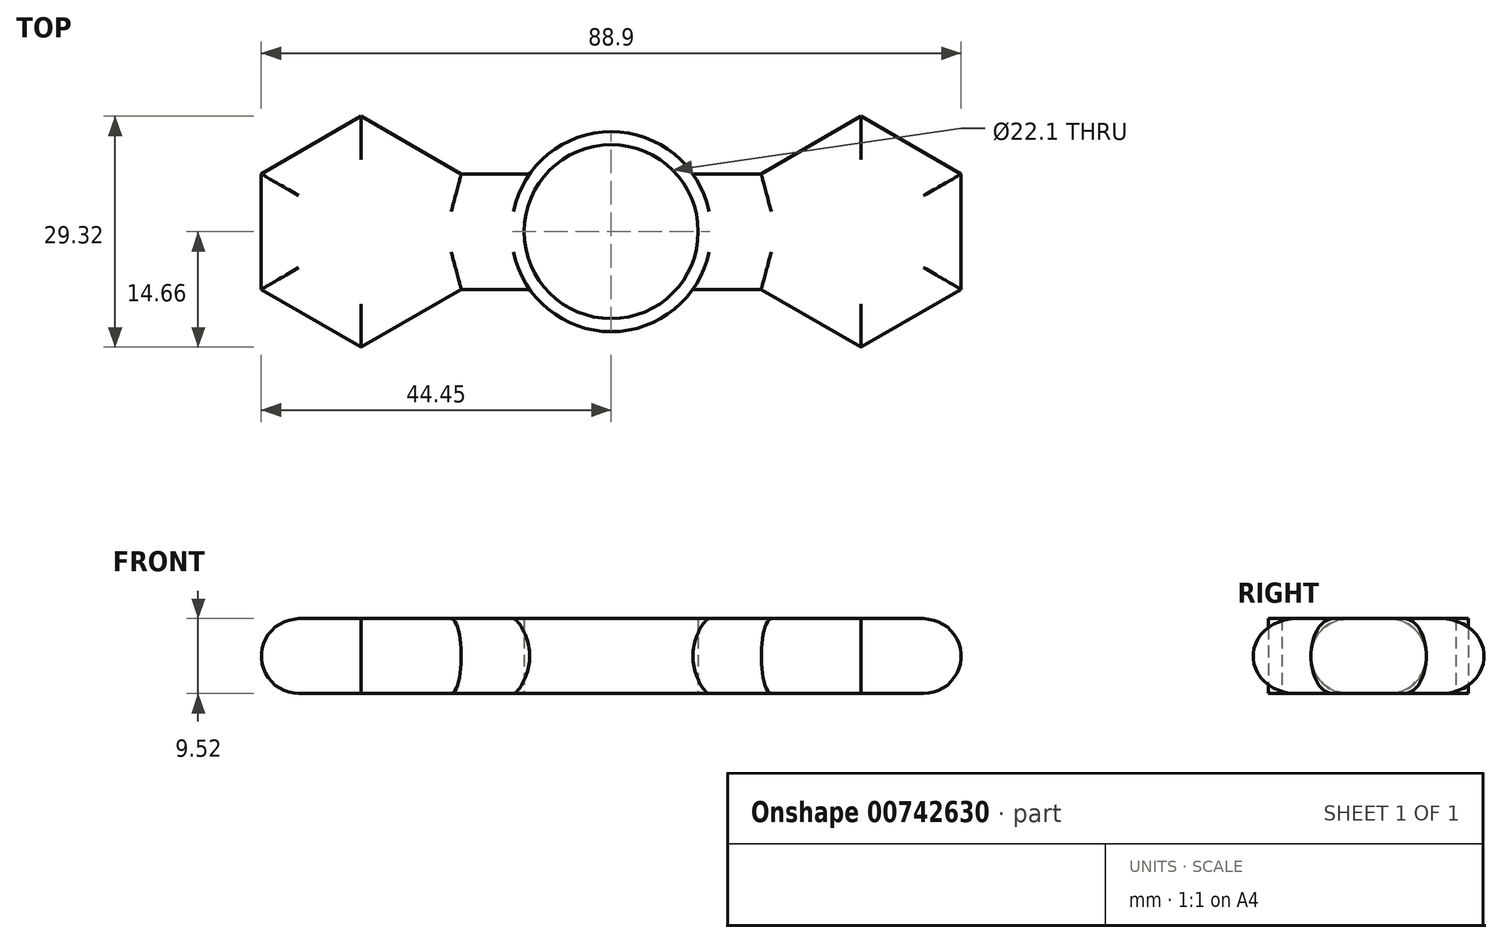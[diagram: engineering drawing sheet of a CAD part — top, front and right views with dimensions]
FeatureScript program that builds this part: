
annotation { "Feature Type Name" : "Feature", "Feature Type Description" : "" }
export const myFeature = defineFeature(function(context is Context, id is Id, definition is map)
    precondition{}
    {
        {
            var Q0;
            Q0=qCreatedBy(makeId("Top.planeOp"),FACE);
            var sketch = newSketch(context, id + "F0", { "sketchPlane" : qUnion([Q0])});
            skCircle(sketch, "E0", {"center": v(0, 0) * mm, "radius": 12.7 * mm});
            skCircle(sketch, "E1", {"center": v(0, 0) * mm, "radius": 11.05 * mm});
            skSolve(sketch);
        }
        {
            var Q0;
            Q0 = qSketchRegion(id + "F0", true);
            extrude(context, id + "F1", {"entities" : qUnion([Q0]), "endBound" : BoundingType.SYMMETRIC, "depth" : 9.52 * mm, "offsetDistance" : 25.4 * mm});
        }
        {
            var Q0;
            Q0=qCreatedBy(makeId("Top.planeOp"),FACE);
            var sketch = newSketch(context, id + "F2", { "sketchPlane" : qUnion([Q0])});
            skArc(sketch, "E2", {"start": v(-10.37, 7.33) * mm, "mid": v(-12.7, 0) * mm, "end": v(-10.37, -7.33) * mm});
            skLineSegment(sketch, "E3.1", {"start": v(-19.05, -7.33) * mm, "end": v(-31.75, -14.66) * mm});
            skLineSegment(sketch, "E3.2", {"start": v(-31.75, -14.66) * mm, "end": v(-44.45, -7.33) * mm});
            skLineSegment(sketch, "E3.3", {"start": v(-44.45, -7.33) * mm, "end": v(-44.45, 7.33) * mm});
            skLineSegment(sketch, "E3.4", {"start": v(-44.45, 7.33) * mm, "end": v(-31.75, 14.66) * mm});
            skLineSegment(sketch, "E3.5", {"start": v(-31.75, 14.66) * mm, "end": v(-19.05, 7.33) * mm});
            skLineSegment(sketch, "E4.MirrorCS", {"start": v(44.45, 7.33) * mm, "end": v(31.75, 14.66) * mm});
            skLineSegment(sketch, "E5.MirrorCS", {"start": v(31.75, 14.66) * mm, "end": v(19.05, 7.33) * mm});
            skLineSegment(sketch, "E6.MirrorCS", {"start": v(44.45, -7.33) * mm, "end": v(44.45, 7.33) * mm});
            skLineSegment(sketch, "E7.MirrorCS", {"start": v(31.75, -14.66) * mm, "end": v(44.45, -7.33) * mm});
            skLineSegment(sketch, "E8.MirrorCS", {"start": v(19.05, -7.33) * mm, "end": v(31.75, -14.66) * mm});
            skLineSegment(sketch, "E9", {"start": v(19.05, 7.33) * mm, "end": v(10.37, 7.33) * mm});
            skLineSegment(sketch, "E10", {"start": v(19.05, -7.33) * mm, "end": v(10.37, -7.33) * mm});
            skLineSegment(sketch, "E11", {"start": v(-19.05, 7.33) * mm, "end": v(-10.37, 7.33) * mm});
            skLineSegment(sketch, "E12", {"start": v(-19.05, -7.33) * mm, "end": v(-10.37, -7.33) * mm});
            skArc(sketch, "E13.trimOffspring", {"start": v(10.37, -7.33) * mm, "mid": v(12.7, 0) * mm, "end": v(10.37, 7.33) * mm});
            skSolve(sketch);
        }
        {
            var Q0;
            Q0 = qSketchRegion(id + "F2", true);
            extrude(context, id + "F3", {"entities" : qUnion([Q0]), "operationType" : NewBodyOperationType.ADD, "endBound" : BoundingType.SYMMETRIC, "depth" : 9.52 * mm, "offsetDistance" : 25.4 * mm});
        }
        {
            var Q0;
            Q0=makeQuery(id+"F3.opExtrude","CAP_EDGE",EDGE,{"disambiguationData":[OSD([sQuery(id+"F2.wireOp",EDGE,"E7.MirrorCS")])],"isStart":false});
            var Q1;
            Q1=makeQuery(id+"F3.opExtrude","CAP_EDGE",EDGE,{"disambiguationData":[OSD([sQuery(id+"F2.wireOp",EDGE,"E6.MirrorCS")])],"isStart":false});
            var Q2;
            Q2=makeQuery(id+"F3.opExtrude","CAP_EDGE",EDGE,{"disambiguationData":[OSD([sQuery(id+"F2.wireOp",EDGE,"E8.MirrorCS")])],"isStart":false});
            var Q3;
            Q3=makeQuery(id+"F3.opExtrude","CAP_EDGE",EDGE,{"disambiguationData":[OSD([sQuery(id+"F2.wireOp",EDGE,"E10")])],"isStart":false});
            var Q4;
            Q4=makeQuery(id+"F3.opExtrude","CAP_EDGE",EDGE,{"disambiguationData":[OSD([sQuery(id+"F2.wireOp",EDGE,"E9")])],"isStart":false});
            var Q5;
            Q5=makeQuery(id+"F3.opExtrude","CAP_EDGE",EDGE,{"disambiguationData":[OSD([sQuery(id+"F2.wireOp",EDGE,"E5.MirrorCS")])],"isStart":false});
            var Q6;
            Q6=makeQuery(id+"F3.opExtrude","CAP_EDGE",EDGE,{"disambiguationData":[OSD([sQuery(id+"F2.wireOp",EDGE,"E4.MirrorCS")])],"isStart":false});
            var Q7;
            Q7=makeQuery(id+"F3.opExtrude","CAP_EDGE",EDGE,{"disambiguationData":[OSD([sQuery(id+"F2.wireOp",EDGE,"E10")])],"isStart":true});
            var Q8;
            Q8=makeQuery(id+"F3.opExtrude","CAP_EDGE",EDGE,{"disambiguationData":[OSD([sQuery(id+"F2.wireOp",EDGE,"E8.MirrorCS")])],"isStart":true});
            var Q9;
            Q9=makeQuery(id+"F3.opExtrude","CAP_EDGE",EDGE,{"disambiguationData":[OSD([sQuery(id+"F2.wireOp",EDGE,"E7.MirrorCS")])],"isStart":true});
            var Q10;
            Q10=makeQuery(id+"F3.opExtrude","CAP_EDGE",EDGE,{"disambiguationData":[OSD([sQuery(id+"F2.wireOp",EDGE,"E6.MirrorCS")])],"isStart":true});
            var Q11;
            Q11=makeQuery(id+"F3.opExtrude","CAP_EDGE",EDGE,{"disambiguationData":[OSD([sQuery(id+"F2.wireOp",EDGE,"E9")])],"isStart":true});
            var Q12;
            Q12=makeQuery(id+"F3.opExtrude","CAP_EDGE",EDGE,{"disambiguationData":[OSD([sQuery(id+"F2.wireOp",EDGE,"E5.MirrorCS")])],"isStart":true});
            var Q13;
            Q13=makeQuery(id+"F3.opExtrude","CAP_EDGE",EDGE,{"disambiguationData":[OSD([sQuery(id+"F2.wireOp",EDGE,"E4.MirrorCS")])],"isStart":true});
            fillet(context, id + "F4", {"entities" : qUnion([Q0, Q1, Q2, Q3, Q4, Q5, Q6, Q7, Q8, Q9, Q10, Q11, Q12, Q13]), "radius" : 4.76 * mm, "tangentPropagation" : true, "allowEdgeOverflow" : false});
        }
        {
            var Q0;
            Q0=makeQuery(id+"F3.opExtrude","CAP_EDGE",EDGE,{"disambiguationData":[OSD([sQuery(id+"F2.wireOp",EDGE,"E3.4")])],"isStart":false});
            var Q1;
            Q1=makeQuery(id+"F3.opExtrude","CAP_EDGE",EDGE,{"disambiguationData":[OSD([sQuery(id+"F2.wireOp",EDGE,"E3.5")])],"isStart":false});
            var Q2;
            Q2=makeQuery(id+"F3.opExtrude","CAP_EDGE",EDGE,{"disambiguationData":[OSD([sQuery(id+"F2.wireOp",EDGE,"E11")])],"isStart":false});
            var Q3;
            Q3=makeQuery(id+"F3.opExtrude","CAP_EDGE",EDGE,{"disambiguationData":[OSD([sQuery(id+"F2.wireOp",EDGE,"E12")])],"isStart":false});
            var Q4;
            Q4=makeQuery(id+"F3.opExtrude","CAP_EDGE",EDGE,{"disambiguationData":[OSD([sQuery(id+"F2.wireOp",EDGE,"E3.1")])],"isStart":false});
            var Q5;
            Q5=makeQuery(id+"F3.opExtrude","CAP_EDGE",EDGE,{"disambiguationData":[OSD([sQuery(id+"F2.wireOp",EDGE,"E3.2")])],"isStart":false});
            var Q6;
            Q6=makeQuery(id+"F3.opExtrude","CAP_EDGE",EDGE,{"disambiguationData":[OSD([sQuery(id+"F2.wireOp",EDGE,"E3.3")])],"isStart":true});
            var Q7;
            Q7=makeQuery(id+"F3.opExtrude","CAP_EDGE",EDGE,{"disambiguationData":[OSD([sQuery(id+"F2.wireOp",EDGE,"E3.3")])],"isStart":false});
            var Q8;
            Q8=makeQuery(id+"F3.opExtrude","CAP_EDGE",EDGE,{"disambiguationData":[OSD([sQuery(id+"F2.wireOp",EDGE,"E3.1")])],"isStart":true});
            var Q9;
            Q9=makeQuery(id+"F3.opExtrude","CAP_EDGE",EDGE,{"disambiguationData":[OSD([sQuery(id+"F2.wireOp",EDGE,"E3.2")])],"isStart":true});
            var Q10;
            Q10=makeQuery(id+"F3.opExtrude","CAP_EDGE",EDGE,{"disambiguationData":[OSD([sQuery(id+"F2.wireOp",EDGE,"E12")])],"isStart":true});
            var Q11;
            Q11=makeQuery(id+"F3.opExtrude","CAP_EDGE",EDGE,{"disambiguationData":[OSD([sQuery(id+"F2.wireOp",EDGE,"E11")])],"isStart":true});
            var Q12;
            Q12=makeQuery(id+"F3.opExtrude","CAP_EDGE",EDGE,{"disambiguationData":[OSD([sQuery(id+"F2.wireOp",EDGE,"E3.5")])],"isStart":true});
            var Q13;
            Q13=makeQuery(id+"F3.opExtrude","CAP_EDGE",EDGE,{"disambiguationData":[OSD([sQuery(id+"F2.wireOp",EDGE,"E3.4")])],"isStart":true});
            fillet(context, id + "F5", {"entities" : qUnion([Q0, Q1, Q2, Q3, Q4, Q5, Q6, Q7, Q8, Q9, Q10, Q11, Q12, Q13]), "radius" : 4.76 * mm, "tangentPropagation" : true, "allowEdgeOverflow" : false});
        }
    });
